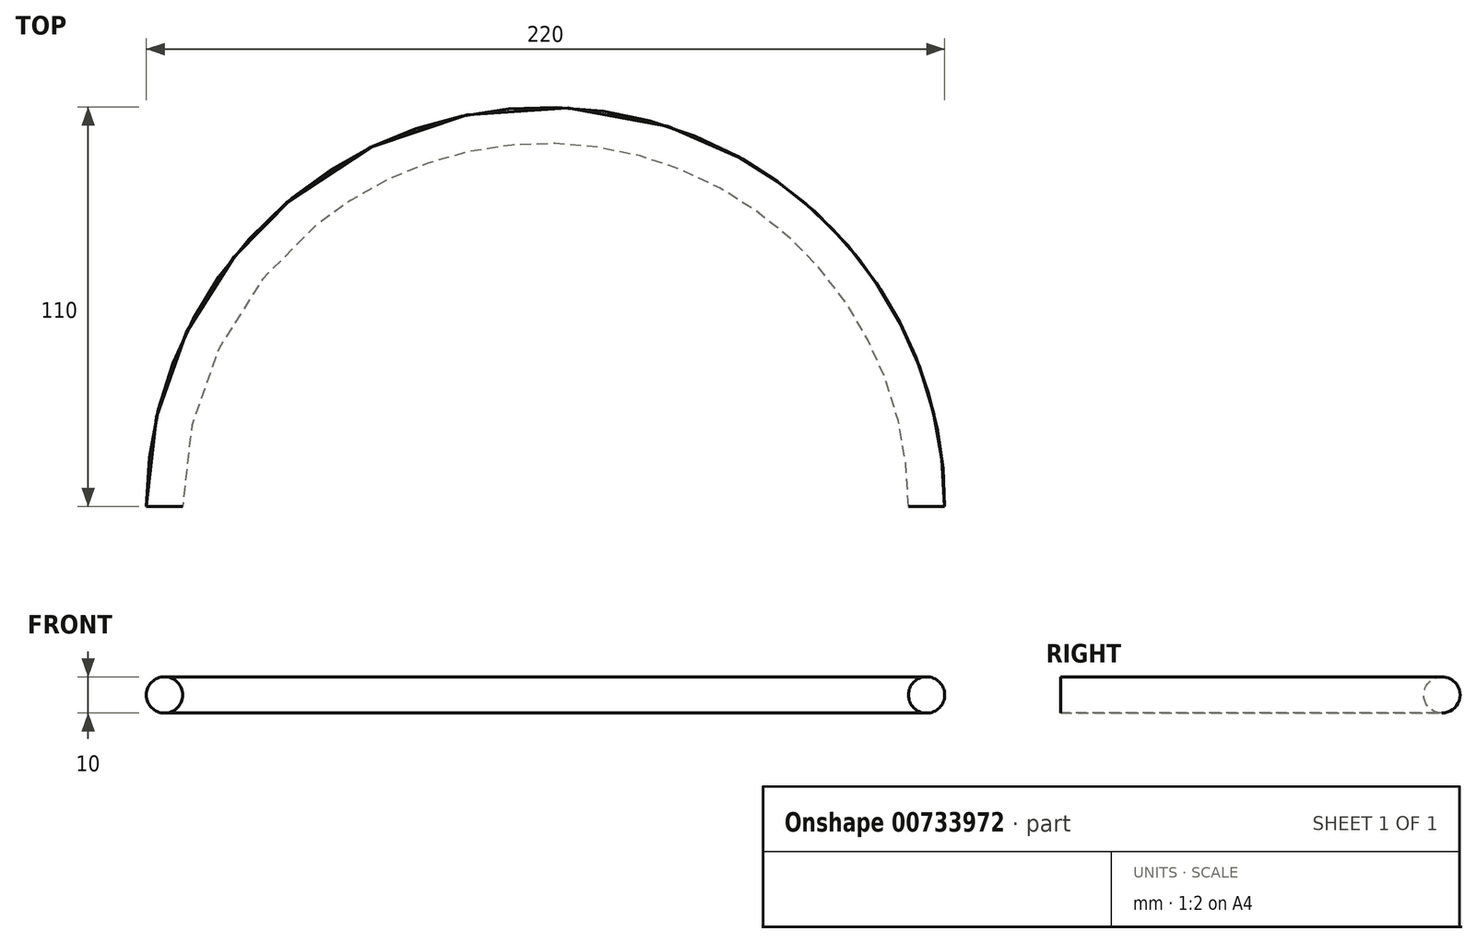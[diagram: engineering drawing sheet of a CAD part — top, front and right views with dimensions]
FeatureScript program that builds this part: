
annotation { "Feature Type Name" : "Feature", "Feature Type Description" : "" }
export const myFeature = defineFeature(function(context is Context, id is Id, definition is map)
    precondition{}
    {
        {
            var Q0;
            Q0=qCreatedBy(makeId("Front.planeOp"),FACE);
            var sketch = newSketch(context, id + "F0", { "sketchPlane" : qUnion([Q0])});
            skCircle(sketch, "E0", {"center": v(-59.28, 0) * mm, "radius": 5 * mm});
            skCircle(sketch, "E1", {"center": v(150.72, 0) * mm, "radius": 5 * mm});
            skSolve(sketch);
        }
        {
            var Q0;
            Q0=qCreatedBy(makeId("Top.planeOp"),FACE);
            var sketch = newSketch(context, id + "F1", { "sketchPlane" : qUnion([Q0])});
            skPoint(sketch, "E2", {"position": v(-59.28, 0) * mm});
            skPoint(sketch, "E3", {"position": v(150.72, 0) * mm});
            skArc(sketch, "E4", {"start": v(-59.28, 0) * mm, "mid": v(45.72, 105) * mm, "end": v(150.72, 0) * mm});
            skSolve(sketch);
        }
        {
            var Q0;
            Q0=makeQuery(id+"F0.imprint","IMPRINT",FACE,{"disambiguationData":[TD([[makeQuery(id+"F0.imprint","IMPRINT",EDGE,{"derivedFrom":sQuery(id+"F0.wireOp",EDGE,"E0")}),1.0]])]});
            var Q1;
            Q1=makeQuery(id+"F0.imprint","IMPRINT",FACE,{"disambiguationData":[TD([[makeQuery(id+"F0.imprint","IMPRINT",EDGE,{"derivedFrom":sQuery(id+"F0.wireOp",EDGE,"E1")}),1.0]])]});
            var Q2;
            Q2=sQuery(id+"F1.wireOp",EDGE,"E4");
            sweep(context, id + "F2", {"profiles" : qUnion([Q0, Q1]), "path" : qUnion([Q2])});
        }
    });
